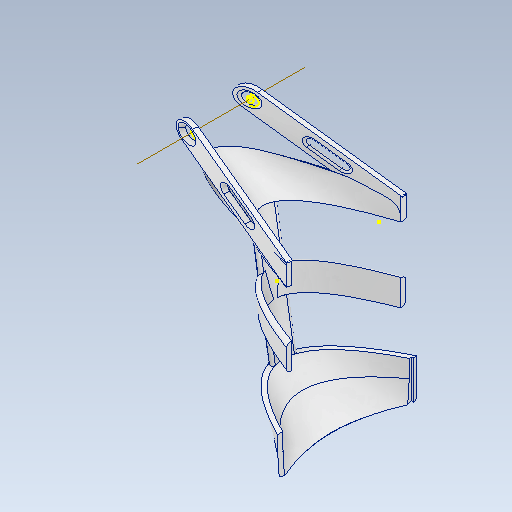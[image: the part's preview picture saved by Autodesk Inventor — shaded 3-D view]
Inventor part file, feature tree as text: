
AUTODESK INVENTOR PART (.ipt)
format: ipt  version: 2021 (Build 250183000, 183)  size: 1,112,064 bytes
history: native  units: mm
features: sketch x37, plane x11, other x4
ambient origin geometry x8: Origin, YZ Plane, XZ Plane, XY Plane, X Axis, Y Axis, Z Axis, Center Point
bodies: Solid1 (feature_tree)
feature tree (52):
  other  "Shoes (upper part)_MIR.ipt"
  other  "Solid1::Shoes (upper part)_MIR.ipt"
  other  "TaggingFeature1"
  sketch  "Sketch1"  dims[d0=10.0mm]
  sketch  "Sketch2"
  sketch  "Sketch3"
  sketch  "Sketch4"
  sketch  "Sketch5"
  sketch  "Sketch6"
  sketch  "Sketch7"
  sketch  "Sketch8"
  sketch  "Sketch9"
  sketch  "Sketch10"
  sketch  "Sketch11"
  sketch  "Sketch12"
  sketch  "Sketch13"
  sketch  "Sketch14"
  sketch  "Sketch15"
  sketch  "Sketch16"
  sketch  "Sketch17"
  sketch  "Sketch18"
  sketch  "Sketch19"
  sketch  "Sketch20"
  sketch  "Sketch21"
  sketch  "Sketch22"
  sketch  "Sketch23"
  sketch  "Sketch24"
  sketch  "Sketch25"
  sketch  "Sketch26"
  sketch  "Sketch27"
  sketch  "Sketch28"
  sketch  "Sketch29"
  sketch  "Sketch30"
  sketch  "Sketch31"
  sketch  "Sketch32"
  sketch  "Sketch33"
  sketch  "Sketch34"
  sketch  "Sketch35"
  sketch  "Sketch36"
  sketch  "3D Sketch1"
  plane  "Work Plane1"
  plane  "Work Plane2"
  plane  "Work Plane3"
  plane  "Work Plane4"
  plane  "Work Plane5"
  plane  "Work Plane6"
  plane  "Work Plane7"
  plane  "Work Plane8"
  plane  "Work Plane9"
  plane  "Work Plane10"
  plane  "Work Plane11"
  other  "Work Axis1"
